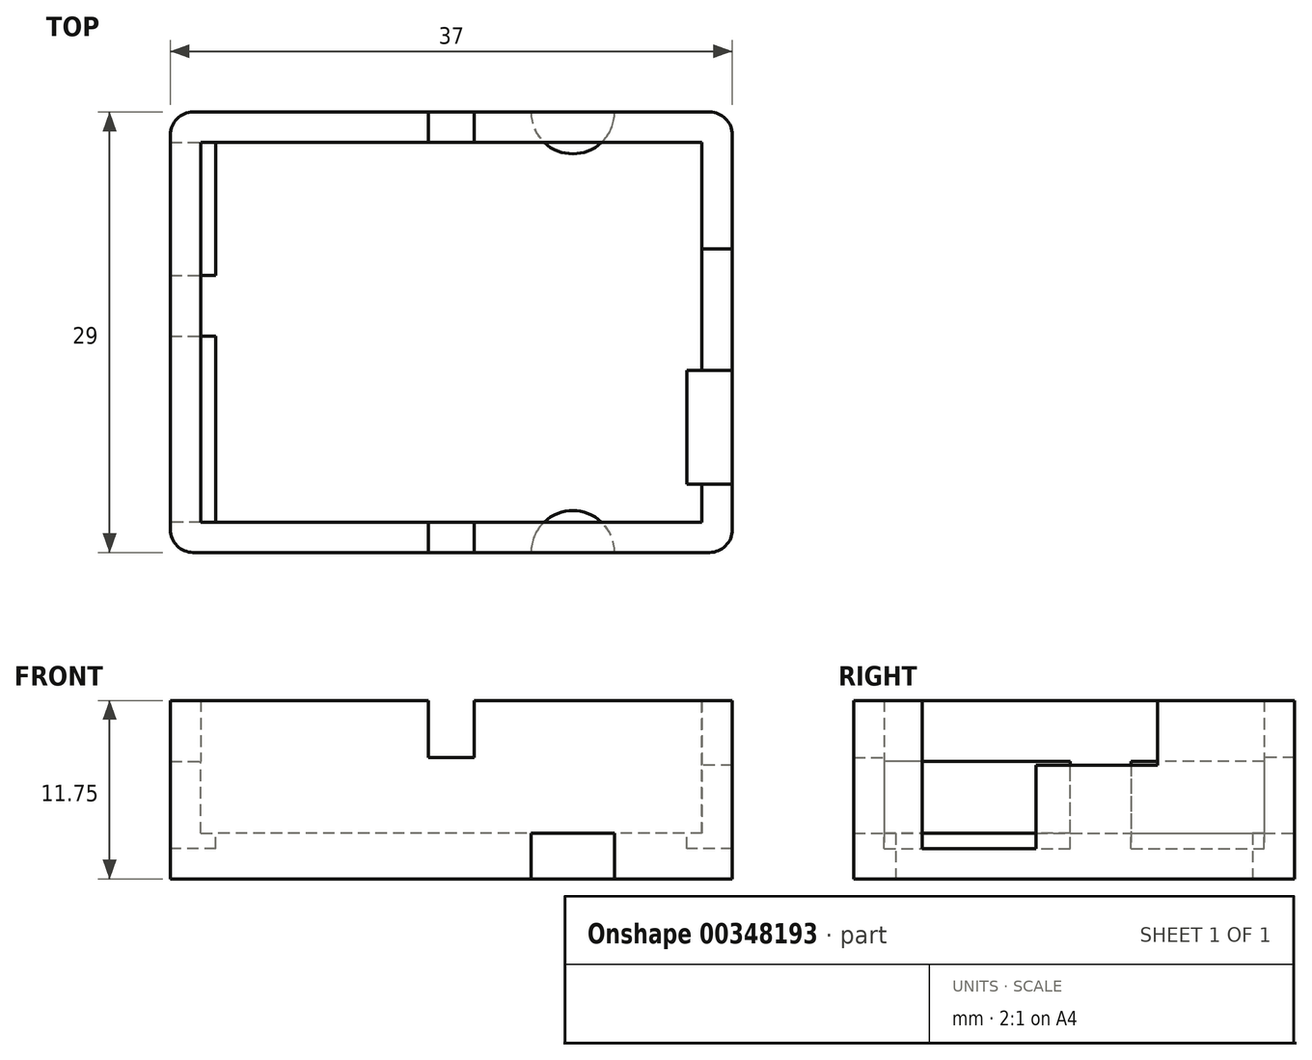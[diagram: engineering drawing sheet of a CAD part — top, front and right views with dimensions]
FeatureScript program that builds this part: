
annotation { "Feature Type Name" : "Feature", "Feature Type Description" : "" }
export const myFeature = defineFeature(function(context is Context, id is Id, definition is map)
    precondition{}
    {
        {
            var Q0;
            Q0=qCreatedBy(makeId("Top.planeOp"),FACE);
            var sketch = newSketch(context, id + "F0", { "sketchPlane" : qUnion([Q0])});
            skPoint(sketch, "E0.middle", {"position": v(0, 0) * mm});
            skLineSegment(sketch, "E1.bottom", {"start": v(16.5, -12.5) * mm, "end": v(-16.5, -12.5) * mm});
            skLineSegment(sketch, "E1.top", {"start": v(16.5, 12.5) * mm, "end": v(-16.5, 12.5) * mm});
            skLineSegment(sketch, "E1.left", {"start": v(16.5, -12.5) * mm, "end": v(16.5, 12.5) * mm});
            skLineSegment(sketch, "E1.right", {"start": v(-16.5, -12.5) * mm, "end": v(-16.5, 12.5) * mm});
            skLineSegment(sketch, "E2.0", {"start": v(18.5, 14.5) * mm, "end": v(-18.5, 14.5) * mm});
            skLineSegment(sketch, "E2.1", {"start": v(18.5, -14.5) * mm, "end": v(18.5, 14.5) * mm});
            skLineSegment(sketch, "E2.2", {"start": v(18.5, -14.5) * mm, "end": v(-18.5, -14.5) * mm});
            skLineSegment(sketch, "E2.3", {"start": v(-18.5, -14.5) * mm, "end": v(-18.5, 14.5) * mm});
            skSolve(sketch);
        }
        {
            var Q0;
            Q0=makeQuery(id+"F0.imprint","IMPRINT",FACE,{"disambiguationData":[TD([[makeQuery(id+"F0.imprint","IMPRINT",EDGE,{"derivedFrom":sQuery(id+"F0.wireOp",EDGE,"E1.bottom")}),1.0]])]});
            extrude(context, id + "F1", {"entities" : qUnion([Q0]), "depth" : 12 * mm});
        }
        {
            var Q0;
            Q0=makeQuery(id+"F0.imprint","IMPRINT",FACE,{"disambiguationData":[TD([[makeQuery(id+"F0.imprint","IMPRINT",EDGE,{"derivedFrom":sQuery(id+"F0.wireOp",EDGE,"E1.bottom")}),-1.0]])]});
            extrude(context, id + "F2", {"entities" : qUnion([Q0]), "operationType" : NewBodyOperationType.ADD, "depth" : 2 * mm});
        }
        {
            var Q0;
            Q0=makeQuery(id+"F1.opExtrude","SWEPT_FACE",FACE,{"disambiguationData":[OSD([sQuery(id+"F0.wireOp",EDGE,"E1.left")])]});
            var sketch = newSketch(context, id + "F3", { "sketchPlane" : qUnion([Q0])});
            skLineSegment(sketch, "E3", {"start": v(12.5, 2) * mm, "end": v(10, 2) * mm});
            skLineSegment(sketch, "E4", {"start": v(10, 2) * mm, "end": v(2.5, 2) * mm});
            skLineSegment(sketch, "E5", {"start": v(2.5, 2) * mm, "end": v(2.5, 7) * mm});
            skLineSegment(sketch, "E6", {"start": v(2.5, 7) * mm, "end": v(-5.5, 7) * mm});
            skLineSegment(sketch, "E7", {"start": v(-5.5, 7) * mm, "end": v(-5.5, 12) * mm});
            skLineSegment(sketch, "E8", {"start": v(-5.5, 12) * mm, "end": v(12.5, 12) * mm});
            skLineSegment(sketch, "E9", {"start": v(12.5, 12) * mm, "end": v(12.5, 2) * mm});
            skLineSegment(sketch, "E10", {"start": v(10, 2) * mm, "end": v(10, 12) * mm});
            skSolve(sketch);
        }
        {
            var Q0;
            Q0=makeQuery(id+"F3.imprint","IMPRINT",FACE,{"disambiguationData":[TD([[makeQuery(id+"F3.imprint","IMPRINT",EDGE,{"derivedFrom":sQuery(id+"F3.wireOp",EDGE,"E4")}),-1.0]])]});
            extrude(context, id + "F4", {"entities" : qUnion([Q0]), "operationType" : NewBodyOperationType.REMOVE, "oppositeDirection" : true, "depth" : 2 * mm});
        }
        {
            var Q0;
            Q0=makeQuery(id+"F4.boolean.opBoolean","MERGE",FACE,{"derivedFrom":[makeQuery(id+"F2.opExtrude","CAP_FACE",FACE,{"disambiguationData":[OSD([sQuery(id+"F0.wireOp",EDGE,"E1.bottom"),sQuery(id+"F0.wireOp",EDGE,"E1.top"),sQuery(id+"F0.wireOp",EDGE,"E1.left"),sQuery(id+"F0.wireOp",EDGE,"E1.right")])],"isStart":false}),makeQuery(id+"F4.opExtrude","SWEPT_FACE",FACE,{"disambiguationData":[OSD([sQuery(id+"F3.wireOp",EDGE,"E4")])]})]});
            var sketch = newSketch(context, id + "F5", { "sketchPlane" : qUnion([Q0])});
            skLineSegment(sketch, "E11", {"start": v(16.5, -10) * mm, "end": v(15.5, -10) * mm});
            skLineSegment(sketch, "E12", {"start": v(16.5, -2.5) * mm, "end": v(15.5, -2.5) * mm});
            skLineSegment(sketch, "E13", {"start": v(15.5, -2.5) * mm, "end": v(15.5, -10) * mm});
            skSolve(sketch);
        }
        {
            var Q0;
            Q0 = qSketchRegion(id + "F5", true);
            var Q1;
            Q1=makeQuery(id+"F5.imprint","IMPRINT",FACE,{"disambiguationData":[TD([[makeQuery(id+"F5.imprint","IMPRINT",EDGE,{"derivedFrom":sQuery(id+"F5.wireOp",EDGE,"E11")}),-1.0]])]});
            extrude(context, id + "F6", {"entities" : qUnion([Q0, Q1]), "operationType" : NewBodyOperationType.REMOVE, "oppositeDirection" : true, "depth" : 1 * mm});
        }
        {
            var Q0;
            Q0=makeQuery(id+"F1.opExtrude","SWEPT_FACE",FACE,{"disambiguationData":[OSD([sQuery(id+"F0.wireOp",EDGE,"E1.right")])]});
            var sketch = newSketch(context, id + "F7", { "sketchPlane" : qUnion([Q0])});
            skLineSegment(sketch, "E14", {"start": v(-12.5, 2) * mm, "end": v(-0.25, 2) * mm});
            skLineSegment(sketch, "E15", {"start": v(-0.25, 2) * mm, "end": v(3.75, 2) * mm});
            skLineSegment(sketch, "E16", {"start": v(3.75, 2) * mm, "end": v(12.5, 2) * mm});
            skLineSegment(sketch, "E17", {"start": v(12.5, 2) * mm, "end": v(12.5, 6.75) * mm});
            skLineSegment(sketch, "E18", {"start": v(12.5, 6.75) * mm, "end": v(3.75, 6.75) * mm});
            skLineSegment(sketch, "E19", {"start": v(3.75, 6.75) * mm, "end": v(3.75, 2) * mm});
            skLineSegment(sketch, "E20", {"start": v(-0.25, 2) * mm, "end": v(-0.25, 6.75) * mm});
            skLineSegment(sketch, "E21", {"start": v(-0.25, 6.75) * mm, "end": v(-12.5, 6.75) * mm});
            skSolve(sketch);
        }
        {
            var Q0;
            Q0 = qSketchRegion(id + "F7", true);
            var Q1;
            {var subQ0=sQuery(id+"F7.wireOp",EDGE,"E14");Q1=makeQuery(id+"F7.imprint","IMPRINT",FACE,{"disambiguationData":[TD([[makeQuery(id+"F7.imprint","IMPRINT",EDGE,{"derivedFrom":subQ0}),1.0]])]});}
            extrude(context, id + "F8", {"entities" : qUnion([Q0, Q1]), "operationType" : NewBodyOperationType.REMOVE, "oppositeDirection" : true, "depth" : 2 * mm});
        }
        {
            var Q0;
            Q0=makeQuery(id+"F8.boolean.opBoolean","MERGE",FACE,{"derivedFrom":[makeQuery(id+"F4.boolean.opBoolean","MERGE",FACE,{"derivedFrom":[makeQuery(id+"F2.opExtrude","CAP_FACE",FACE,{"disambiguationData":[OSD([sQuery(id+"F0.wireOp",EDGE,"E1.bottom"),sQuery(id+"F0.wireOp",EDGE,"E1.top"),sQuery(id+"F0.wireOp",EDGE,"E1.left"),sQuery(id+"F0.wireOp",EDGE,"E1.right")])],"isStart":false}),makeQuery(id+"F4.opExtrude","SWEPT_FACE",FACE,{"disambiguationData":[OSD([sQuery(id+"F3.wireOp",EDGE,"E4")])]})]}),makeQuery(id+"F8.opExtrude","SWEPT_FACE",FACE,{"disambiguationData":[OSD([sQuery(id+"F7.wireOp",EDGE,"E14")])]}),makeQuery(id+"F8.opExtrude","SWEPT_FACE",FACE,{"disambiguationData":[OSD([sQuery(id+"F7.wireOp",EDGE,"E16")])]})]});
            var sketch = newSketch(context, id + "F9", { "sketchPlane" : qUnion([Q0])});
            skLineSegment(sketch, "E22", {"start": v(-16.5, -0.25) * mm, "end": v(-15.5, -0.25) * mm});
            skLineSegment(sketch, "E23", {"start": v(-15.5, -0.25) * mm, "end": v(-15.5, -12.5) * mm});
            skLineSegment(sketch, "E24", {"start": v(-16.5, 3.75) * mm, "end": v(-15.5, 3.75) * mm});
            skLineSegment(sketch, "E25", {"start": v(-15.5, 3.75) * mm, "end": v(-15.5, 12.5) * mm});
            skSolve(sketch);
        }
        {
            var Q0;
            Q0 = qSketchRegion(id + "F9", true);
            var Q1;
            Q1=makeQuery(id+"F9.imprint","IMPRINT",FACE,{"disambiguationData":[TD([[makeQuery(id+"F9.imprint","IMPRINT",EDGE,{"derivedFrom":sQuery(id+"F9.wireOp",EDGE,"E24")}),1.0]])]});
            var Q2;
            Q2=makeQuery(id+"F9.imprint","IMPRINT",FACE,{"disambiguationData":[TD([[makeQuery(id+"F9.imprint","IMPRINT",EDGE,{"derivedFrom":sQuery(id+"F9.wireOp",EDGE,"E22")}),-1.0]])]});
            extrude(context, id + "F10", {"entities" : qUnion([Q0, Q1, Q2]), "operationType" : NewBodyOperationType.REMOVE, "oppositeDirection" : true, "depth" : 1 * mm});
        }
        {
            var Q0;
            {var subQ0=sQuery(id+"F0.wireOp",EDGE,"E1.right");var subQ1=sQuery(id+"F0.wireOp",EDGE,"E1.left");var subQ2=sQuery(id+"F0.wireOp",EDGE,"E1.top");var subQ3=sQuery(id+"F0.wireOp",EDGE,"E1.bottom");Q0=makeQuery(id+"F2.boolean.opBoolean","MERGE",FACE,{"derivedFrom":[makeQuery(id+"F1.opExtrude","CAP_FACE",FACE,{"disambiguationData":[OSD([subQ3,subQ2,subQ1,subQ0,sQuery(id+"F0.wireOp",EDGE,"E2.0"),sQuery(id+"F0.wireOp",EDGE,"E2.1"),sQuery(id+"F0.wireOp",EDGE,"E2.2"),sQuery(id+"F0.wireOp",EDGE,"E2.3")])],"isStart":true}),makeQuery(id+"F2.opExtrude","CAP_FACE",FACE,{"disambiguationData":[OSD([subQ3,subQ2,subQ1,subQ0])],"isStart":true})]});}
            extrude(context, id + "F11", {"entities" : qUnion([Q0]), "operationType" : NewBodyOperationType.ADD, "depth" : 1 * mm});
        }
        {
            var Q0;
            Q0=makeQuery(id+"F11.opExtrude","CAP_FACE",FACE,{"disambiguationData":[OSD([sQuery(id+"F0.wireOp",EDGE,"E1.bottom"),sQuery(id+"F0.wireOp",EDGE,"E1.top"),sQuery(id+"F0.wireOp",EDGE,"E1.left"),sQuery(id+"F0.wireOp",EDGE,"E1.right"),sQuery(id+"F0.wireOp",EDGE,"E2.0"),sQuery(id+"F0.wireOp",EDGE,"E2.1"),sQuery(id+"F0.wireOp",EDGE,"E2.2"),sQuery(id+"F0.wireOp",EDGE,"E2.3")])],"isStart":false});
            var sketch = newSketch(context, id + "F12", { "sketchPlane" : qUnion([Q0])});
            skLineSegment(sketch, "E26", {"start": v(18.5, 14.5) * mm, "end": v(8, 14.5) * mm});
            skLineSegment(sketch, "E27", {"start": v(18.5, -14.5) * mm, "end": v(8, -14.5) * mm});
            skArc(sketch, "E28", {"start": v(5.25, 14.5) * mm, "mid": v(8, 11.75) * mm, "end": v(10.75, 14.5) * mm});
            skArc(sketch, "E29", {"start": v(10.75, -14.5) * mm, "mid": v(8, -11.75) * mm, "end": v(5.25, -14.5) * mm});
            skSolve(sketch);
        }
        {
            var Q0;
            Q0 = qSketchRegion(id + "F12", true);
            var Q1;
            {var subQ3=sQuery(id+"F12.wireOp",EDGE,"E28");Q1=makeQuery(id+"F12.imprint","IMPRINT",FACE,{"disambiguationData":[TD([[makeQuery(id+"F12.imprint","IMPRINT",EDGE,{"derivedFrom":subQ3}),1.0]])]});}
            var Q2;
            {var subQ3=sQuery(id+"F12.wireOp",EDGE,"E29");Q2=makeQuery(id+"F12.imprint","IMPRINT",FACE,{"disambiguationData":[TD([[makeQuery(id+"F12.imprint","IMPRINT",EDGE,{"derivedFrom":subQ3}),1.0]])]});}
            extrude(context, id + "F13", {"entities" : qUnion([Q0, Q1, Q2]), "operationType" : NewBodyOperationType.REMOVE, "oppositeDirection" : true, "depth" : 3 * mm});
        }
        {
            var Q0;
            {var subQ0=sQuery(id+"F0.wireOp",EDGE,"E2.3");var subQ1=sQuery(id+"F0.wireOp",EDGE,"E2.2");Q0=makeQuery(id+"F11.boolean.opBoolean","MERGE",EDGE,{"derivedFrom":[makeQuery(id+"F1.opExtrude","SWEPT_EDGE",EDGE,{"disambiguationData":[OSD([subQ1,subQ0])]}),makeQuery(id+"F11.opExtrude","SWEPT_EDGE",EDGE,{"disambiguationData":[OSD([subQ1,subQ0])]})]});}
            var Q1;
            {var subQ0=sQuery(id+"F0.wireOp",EDGE,"E2.2");var subQ1=sQuery(id+"F0.wireOp",EDGE,"E2.1");Q1=makeQuery(id+"F11.boolean.opBoolean","MERGE",EDGE,{"derivedFrom":[makeQuery(id+"F1.opExtrude","SWEPT_EDGE",EDGE,{"disambiguationData":[OSD([subQ1,subQ0])]}),makeQuery(id+"F11.opExtrude","SWEPT_EDGE",EDGE,{"disambiguationData":[OSD([subQ1,subQ0])]})]});}
            var Q2;
            {var subQ0=sQuery(id+"F0.wireOp",EDGE,"E2.1");var subQ1=sQuery(id+"F0.wireOp",EDGE,"E2.0");Q2=makeQuery(id+"F11.boolean.opBoolean","MERGE",EDGE,{"derivedFrom":[makeQuery(id+"F1.opExtrude","SWEPT_EDGE",EDGE,{"disambiguationData":[OSD([subQ1,subQ0])]}),makeQuery(id+"F11.opExtrude","SWEPT_EDGE",EDGE,{"disambiguationData":[OSD([subQ1,subQ0])]})]});}
            var Q3;
            {var subQ0=sQuery(id+"F0.wireOp",EDGE,"E2.3");var subQ1=sQuery(id+"F0.wireOp",EDGE,"E2.0");Q3=makeQuery(id+"F11.boolean.opBoolean","MERGE",EDGE,{"derivedFrom":[makeQuery(id+"F1.opExtrude","SWEPT_EDGE",EDGE,{"disambiguationData":[OSD([subQ1,subQ0])]}),makeQuery(id+"F11.opExtrude","SWEPT_EDGE",EDGE,{"disambiguationData":[OSD([subQ1,subQ0])]})]});}
            fillet(context, id + "F14", {"entities" : qUnion([Q0, Q1, Q2, Q3]), "radius" : 1.5 * mm, "tangentPropagation" : true, "allowEdgeOverflow" : false});
        }
        {
            var Q0;
            {var subQ0=sQuery(id+"F7.wireOp",EDGE,"E17");var subQ1=sQuery(id+"F0.wireOp",EDGE,"E1.top");Q0=makeQuery(id+"F10.boolean.opBoolean","MERGE",FACE,{"derivedFrom":[makeQuery(id+"F8.boolean.opBoolean","MERGE",FACE,{"derivedFrom":[makeQuery(id+"F1.opExtrude","SWEPT_FACE",FACE,{"disambiguationData":[OSD([subQ1])]}),makeQuery(id+"F8.opExtrude","SWEPT_FACE",FACE,{"disambiguationData":[OSD([subQ0])]})]}),makeQuery(id+"F10.opExtrude","SWEPT_FACE",FACE,{"disambiguationData":[OSD([subQ1,sQuery(id+"F7.wireOp",EDGE,"E16"),subQ0])]})]});}
            var sketch = newSketch(context, id + "F15", { "sketchPlane" : qUnion([Q0])});
            skLineSegment(sketch, "E30", {"start": v(-16.5, 12) * mm, "end": v(-1.5, 12) * mm});
            skLineSegment(sketch, "E31", {"start": v(-1.5, 12) * mm, "end": v(1.5, 12) * mm});
            skLineSegment(sketch, "E32", {"start": v(1.5, 12) * mm, "end": v(16.5, 12) * mm});
            skLineSegment(sketch, "E33", {"start": v(-1.5, 12) * mm, "end": v(-1.5, 8.5) * mm});
            skLineSegment(sketch, "E34", {"start": v(-1.5, 8.5) * mm, "end": v(1.5, 8.5) * mm});
            skLineSegment(sketch, "E35", {"start": v(1.5, 8.5) * mm, "end": v(1.5, 12) * mm});
            skSolve(sketch);
        }
        {
            var Q0;
            Q0 = qSketchRegion(id + "F15", true);
            extrude(context, id + "F16", {"entities" : qUnion([Q0]), "operationType" : NewBodyOperationType.REMOVE, "depth" : 27 * mm});
        }
        {
            var Q0;
            Q0 = qSketchRegion(id + "F15", true);
            extrude(context, id + "F17", {"entities" : qUnion([Q0]), "operationType" : NewBodyOperationType.REMOVE, "oppositeDirection" : true, "depth" : 2 * mm});
        }
        {
            var Q0;
            Q0=makeQuery(id+"F4.boolean.opBoolean","COPY",FACE,{"derivedFrom":makeQuery(id+"F4.opExtrude","SWEPT_FACE",FACE,{"disambiguationData":[OSD([sQuery(id+"F3.wireOp",EDGE,"E6")])]})});
            extrude(context, id + "F18", {"entities" : qUnion([Q0]), "operationType" : NewBodyOperationType.REMOVE, "oppositeDirection" : true, "depth" : .5 * mm});
        }
        {
            var Q0;
            {var subQ0=sQuery(id+"F0.wireOp",EDGE,"E2.2");var subQ1=sQuery(id+"F3.wireOp",EDGE,"E10");var subQ2=sQuery(id+"F0.wireOp",EDGE,"E1.right");var subQ3=sQuery(id+"F0.wireOp",EDGE,"E1.bottom");var subQ4=sQuery(id+"F0.wireOp",EDGE,"E2.1");var subQ5=sQuery(id+"F0.wireOp",EDGE,"E1.left");Q0=makeQuery(id+"F16.boolean.opBoolean","SPLIT",FACE,{"disambiguationData":[TD([makeQuery(id+"F4.boolean.opBoolean","COPY",FACE,{"derivedFrom":makeQuery(id+"F4.opExtrude","SWEPT_FACE",FACE,{"disambiguationData":[OSD([subQ1])]})})])],"derivedFrom":makeQuery(id+"F1.opExtrude","CAP_FACE",FACE,{"disambiguationData":[OSD([subQ3,sQuery(id+"F0.wireOp",EDGE,"E1.top"),subQ5,subQ2,sQuery(id+"F0.wireOp",EDGE,"E2.0"),subQ4,subQ0,sQuery(id+"F0.wireOp",EDGE,"E2.3")])],"isStart":false})});}
            var Q1;
            {var subQ0=sQuery(id+"F0.wireOp",EDGE,"E2.1");var subQ1=sQuery(id+"F0.wireOp",EDGE,"E2.0");var subQ7=sQuery(id+"F0.wireOp",EDGE,"E1.top");var subQ9=makeQuery(id+"F1.opExtrude","SWEPT_FACE",FACE,{"disambiguationData":[OSD([subQ7])]});var subQ11=sQuery(id+"F0.wireOp",EDGE,"E1.left");var subQ12=makeQuery(id+"F1.opExtrude","SWEPT_FACE",FACE,{"disambiguationData":[OSD([subQ11])]});var subQ15=sQuery(id+"F0.wireOp",EDGE,"E2.3");var subQ16=sQuery(id+"F0.wireOp",EDGE,"E2.2");var subQ17=sQuery(id+"F0.wireOp",EDGE,"E1.bottom");var subQ18=sQuery(id+"F0.wireOp",EDGE,"E1.right");Q1=makeQuery(id+"F17.boolean.opBoolean","SPLIT",FACE,{"disambiguationData":[TD([subQ12])],"derivedFrom":makeQuery(id+"F16.boolean.opBoolean","SPLIT",FACE,{"disambiguationData":[TD([subQ9])],"derivedFrom":makeQuery(id+"F1.opExtrude","CAP_FACE",FACE,{"disambiguationData":[OSD([subQ17,subQ7,subQ11,subQ18,subQ1,subQ0,subQ16,subQ15])],"isStart":false})})});}
            var Q2;
            {var subQ1=sQuery(id+"F0.wireOp",EDGE,"E1.top");var subQ3=makeQuery(id+"F1.opExtrude","SWEPT_FACE",FACE,{"disambiguationData":[OSD([subQ1])]});var subQ4=sQuery(id+"F0.wireOp",EDGE,"E1.right");var subQ5=sQuery(id+"F0.wireOp",EDGE,"E1.bottom");var subQ7=sQuery(id+"F0.wireOp",EDGE,"E2.3");var subQ11=sQuery(id+"F0.wireOp",EDGE,"E2.2");var subQ16=makeQuery(id+"F1.opExtrude","SWEPT_FACE",FACE,{"disambiguationData":[OSD([subQ5])]});var subQ18=sQuery(id+"F0.wireOp",EDGE,"E2.0");var subQ24=sQuery(id+"F0.wireOp",EDGE,"E2.1");var subQ25=sQuery(id+"F0.wireOp",EDGE,"E1.left");Q2=makeQuery(id+"F17.boolean.opBoolean","SPLIT",FACE,{"disambiguationData":[TD([subQ16])],"derivedFrom":makeQuery(id+"F16.boolean.opBoolean","SPLIT",FACE,{"disambiguationData":[TD([subQ3])],"derivedFrom":makeQuery(id+"F1.opExtrude","CAP_FACE",FACE,{"disambiguationData":[OSD([subQ5,subQ1,subQ25,subQ4,subQ18,subQ24,subQ11,subQ7])],"isStart":false})})});}
            extrude(context, id + "F19", {"entities" : qUnion([Q0, Q1, Q2]), "operationType" : NewBodyOperationType.REMOVE, "oppositeDirection" : true, "depth" : 1.25 * mm});
        }
        {
            var Q0;
            Q0=makeQuery(id+"F16.boolean.opBoolean","COPY",FACE,{"derivedFrom":makeQuery(id+"F16.opExtrude","SWEPT_FACE",FACE,{"disambiguationData":[OSD([sQuery(id+"F15.wireOp",EDGE,"E34")])]})});
            var Q1;
            Q1=makeQuery(id+"F17.boolean.opBoolean","COPY",FACE,{"derivedFrom":makeQuery(id+"F17.opExtrude","SWEPT_FACE",FACE,{"disambiguationData":[OSD([sQuery(id+"F15.wireOp",EDGE,"E34")])]})});
            extrude(context, id + "F20", {"entities" : qUnion([Q0, Q1]), "operationType" : NewBodyOperationType.REMOVE, "oppositeDirection" : true, "depth" : 1.5 * mm});
        }
    });
